# Revit family: Corner Units
name_source: partatom
category: Furniture
units: mm (PartAtom-declared; Revit-internal decimal feet)

## family parameters
Always vertical = Yes
Cut with Voids When Loaded = No
OmniClass Number = 23.40.20.00
OmniClass Title = General Furniture and Specialties
Room Calculation Point = No
Shared = No
Work Plane-Based = No

## types (12) — shared parameters
Default Elevation = 0' - 0"
Manufacturer = AIS Inc
Product = CORNER UNITS
URL = https://www.ais-inc.com

## per-type parameters (varying)
| type | Description |
| F-SCCR343030L | 30Wx30Dx34H Configurable LB Lounge Left Corner Unit Solid Base (3-Cushion) |
| F-SCCR343030R | 30Wx30Dx34H Configurable LB Lounge Right Corner Unit Solid Base (3-Cushion) |
| F-SCCR423030L | 30Wx30Dx42H Configurable LB Lounge Left Corner Unit Solid Base (3-Cushion) |
| F-SCCR423030R | 30Wx30Dx42H Configurable LB Lounge Right Corner Unit Solid Base (3-Cushion) |
| F-SCCR503030L | 30Wx30Dx50H Configurable LB Lounge Left Corner Unit Solid Base (3-Cushion) |
| F-SCCR503030R | 30Wx30Dx50H Configurable LB Lounge Right Corner Unit Solid Base (3-Cushion) |
| F-SSCR343030L | 30Wx30Dx34H Configurable LB Lounge Left Corner Unit Open Base (3-Cushion) |
| F-SSCR343030R | 30Wx30Dx34H Configurable LB Lounge Right Corner Unit Open Base (3-Cushion) |
| F-SSCR423030L | 30Wx30Dx42H Configurable LB Lounge Left Corner Unit Open Base (3-Cushion) |
| F-SSCR423030R | 30Wx30Dx42H Configurable LB Lounge Right Corner Unit Open Base (3-Cushion) |
| F-SSCR503030L | 30Wx30Dx50H Configurable LB Lounge Left Corner Unit Open Base (3-Cushion) |
| F-SSCR503030R | 30Wx30Dx50H Configurable LB Lounge Right Corner Unit Open Base (3-Cushion) |

note: column(s) folded — value = type name in every type: Model

type visibility flags: 12 boolean params named "<type name>" — each type sets only its own to Yes (folded from table)

## geometry (parser evidence)
native form markers: Sweep x3
no freeform markers — native parametric forms only
